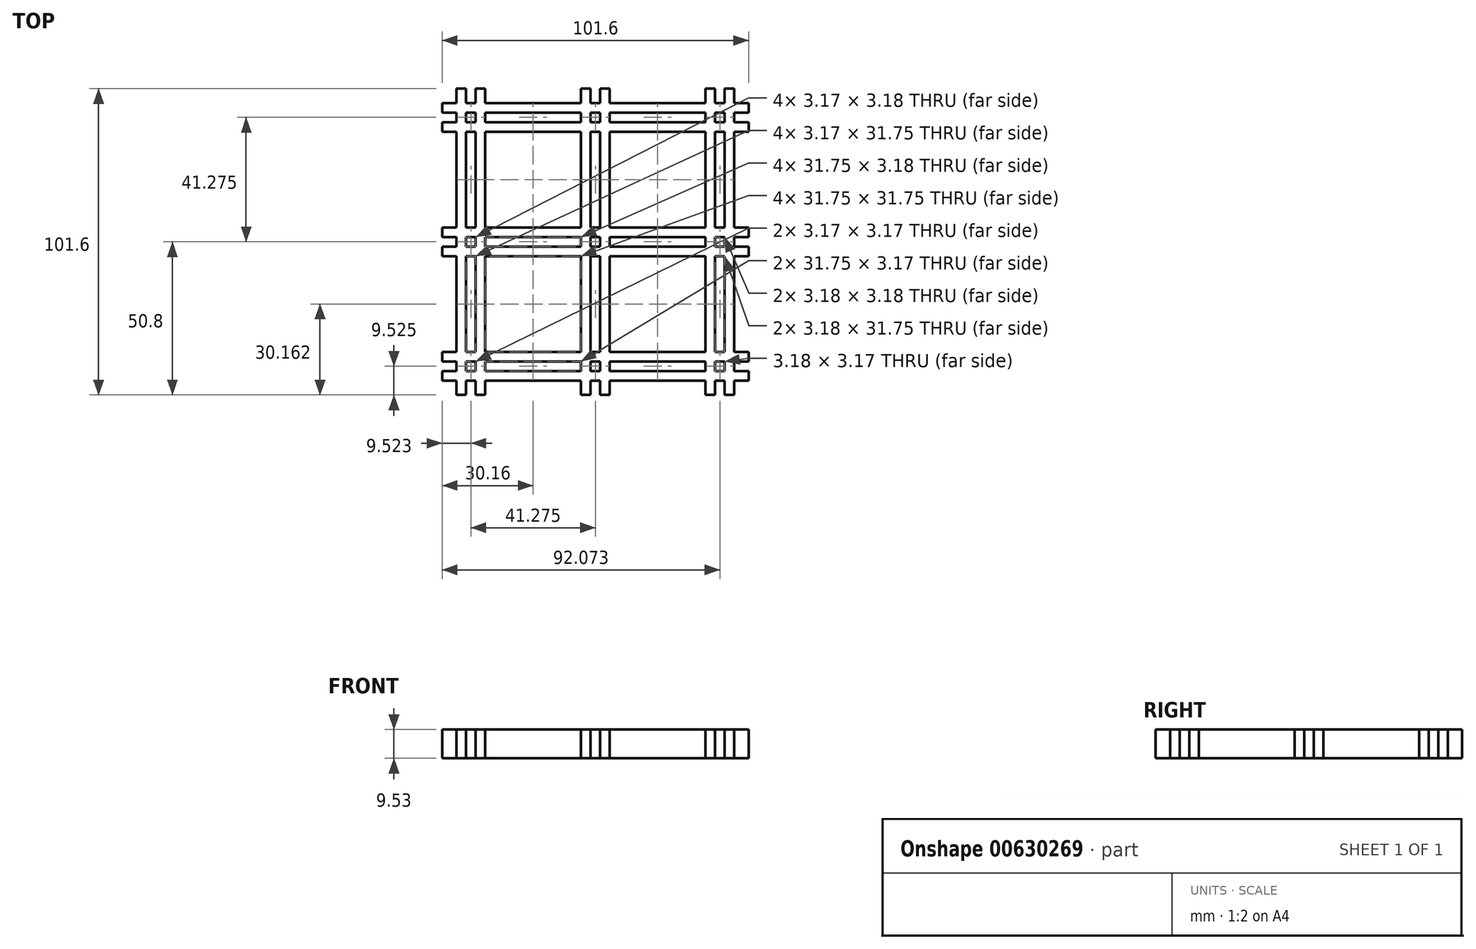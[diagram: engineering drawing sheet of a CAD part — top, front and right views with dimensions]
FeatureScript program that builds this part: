
annotation { "Feature Type Name" : "Feature", "Feature Type Description" : "" }
export const myFeature = defineFeature(function(context is Context, id is Id, definition is map)
    precondition{}
    {
        {
            var Q0;
            Q0=qCreatedBy(makeId("Top.planeOp"),FACE);
            var sketch = newSketch(context, id + "F0", { "sketchPlane" : qUnion([Q0])});
            skLineSegment(sketch, "E0.bottom", {"start": v(0, 0) * mm, "end": v(3.17, 0) * mm});
            skLineSegment(sketch, "E0.top", {"start": v(0, -101.6) * mm, "end": v(3.18, -101.6) * mm});
            skLineSegment(sketch, "E0.left", {"start": v(0, 0) * mm, "end": v(0, -101.6) * mm});
            skLineSegment(sketch, "E0.right", {"start": v(3.17, 0) * mm, "end": v(3.17, -101.6) * mm});
            skLineSegment(sketch, "E1.bottom", {"start": v(6.35, 0) * mm, "end": v(9.52, 0) * mm});
            skLineSegment(sketch, "E1.top", {"start": v(6.35, -101.6) * mm, "end": v(9.53, -101.6) * mm});
            skLineSegment(sketch, "E1.left", {"start": v(6.35, 0) * mm, "end": v(6.35, -101.6) * mm});
            skLineSegment(sketch, "E1.right", {"start": v(9.53, 0) * mm, "end": v(9.53, -101.6) * mm});
            skLineSegment(sketch, "E2.bottom", {"start": v(41.27, 0) * mm, "end": v(44.45, 0) * mm});
            skLineSegment(sketch, "E2.top", {"start": v(41.28, -101.6) * mm, "end": v(44.45, -101.6) * mm});
            skLineSegment(sketch, "E2.left", {"start": v(41.27, 0) * mm, "end": v(41.28, -101.6) * mm});
            skLineSegment(sketch, "E2.right", {"start": v(44.45, 0) * mm, "end": v(44.45, -101.6) * mm});
            skLineSegment(sketch, "E3", {"start": v(3.17, 0) * mm, "end": v(6.35, 0) * mm, "construction": true});
            skLineSegment(sketch, "E4", {"start": v(9.52, 0) * mm, "end": v(41.27, 0) * mm, "construction": true});
            skLineSegment(sketch, "E5.bottom", {"start": v(47.62, 0) * mm, "end": v(50.8, 0) * mm});
            skLineSegment(sketch, "E5.top", {"start": v(47.62, -101.6) * mm, "end": v(50.8, -101.6) * mm});
            skLineSegment(sketch, "E5.left", {"start": v(47.62, 0) * mm, "end": v(47.62, -101.6) * mm});
            skLineSegment(sketch, "E5.right", {"start": v(50.8, 0) * mm, "end": v(50.8, -101.6) * mm});
            skLineSegment(sketch, "E6.bottom", {"start": v(82.55, -101.6) * mm, "end": v(85.73, -101.6) * mm});
            skLineSegment(sketch, "E6.top", {"start": v(82.55, 0) * mm, "end": v(85.72, 0) * mm});
            skLineSegment(sketch, "E6.left", {"start": v(82.55, -101.6) * mm, "end": v(82.55, 0) * mm});
            skLineSegment(sketch, "E6.right", {"start": v(85.73, -101.6) * mm, "end": v(85.72, 0) * mm});
            skLineSegment(sketch, "E7.bottom", {"start": v(88.9, 0) * mm, "end": v(92.07, 0) * mm});
            skLineSegment(sketch, "E7.top", {"start": v(88.9, -101.6) * mm, "end": v(92.07, -101.6) * mm});
            skLineSegment(sketch, "E7.left", {"start": v(88.9, 0) * mm, "end": v(88.9, -101.6) * mm});
            skLineSegment(sketch, "E7.right", {"start": v(92.07, 0) * mm, "end": v(92.07, -101.6) * mm});
            skLineSegment(sketch, "E8", {"start": v(44.45, 0) * mm, "end": v(47.62, 0) * mm, "construction": true});
            skLineSegment(sketch, "E9", {"start": v(50.8, 0) * mm, "end": v(82.55, 0) * mm, "construction": true});
            skLineSegment(sketch, "E10", {"start": v(85.72, 0) * mm, "end": v(88.9, 0) * mm, "construction": true});
            skSolve(sketch);
        }
        {
            var Q0;
            Q0=qSketchRegion(id+"F0",true);
            extrude(context, id + "F1", {"entities" : qUnion([Q0]), "depth" : 9.52 * mm, "offsetDistance" : 25.4 * mm});
        }
        {
            var Q0;
            Q0=makeQuery(id+"F1.opExtrude","SWEPT_FACE",FACE,{"disambiguationData":[OSD([sQuery(id+"F0.wireOp",EDGE,"E7.right")])]});
            var sketch = newSketch(context, id + "F2", { "sketchPlane" : qUnion([Q0])});
            skLineSegment(sketch, "E11.bottom", {"start": v(-96.84, 0) * mm, "end": v(-93.66, 0) * mm});
            skLineSegment(sketch, "E11.top", {"start": v(-96.84, 4.76) * mm, "end": v(-93.66, 4.76) * mm});
            skLineSegment(sketch, "E11.left", {"start": v(-96.84, 0) * mm, "end": v(-96.84, 4.76) * mm});
            skLineSegment(sketch, "E11.right", {"start": v(-93.66, 0) * mm, "end": v(-93.66, 4.76) * mm});
            skLineSegment(sketch, "E12.top", {"start": v(-52.39, 4.76) * mm, "end": v(-49.21, 4.76) * mm, "construction": true});
            skLineSegment(sketch, "E12.left", {"start": v(-49.21, 0) * mm, "end": v(-49.21, 4.76) * mm});
            skLineSegment(sketch, "E12.right", {"start": v(-52.39, 0) * mm, "end": v(-52.39, 4.76) * mm});
            skLineSegment(sketch, "E13.bottom", {"start": v(-7.94, 0) * mm, "end": v(-4.76, 0) * mm});
            skLineSegment(sketch, "E13.top", {"start": v(-7.94, 4.76) * mm, "end": v(-4.76, 4.76) * mm});
            skLineSegment(sketch, "E13.left", {"start": v(-7.94, 0) * mm, "end": v(-7.94, 4.76) * mm});
            skLineSegment(sketch, "E13.right", {"start": v(-4.76, 0) * mm, "end": v(-4.76, 4.76) * mm});
            skLineSegment(sketch, "E14", {"start": v(-50.8, 4.76) * mm, "end": v(-50.8, 9.53) * mm, "construction": true});
            skLineSegment(sketch, "E15", {"start": v(-52.39, 4.76) * mm, "end": v(-55.56, 4.76) * mm});
            skLineSegment(sketch, "E16", {"start": v(-55.56, 4.76) * mm, "end": v(-55.56, 0) * mm});
            skLineSegment(sketch, "E17", {"start": v(-55.56, 0) * mm, "end": v(-52.39, 0) * mm});
            skLineSegment(sketch, "E18", {"start": v(-49.21, 0) * mm, "end": v(-46.04, 0) * mm});
            skLineSegment(sketch, "E19", {"start": v(-46.04, 0) * mm, "end": v(-46.04, 4.76) * mm});
            skLineSegment(sketch, "E20", {"start": v(-46.04, 4.76) * mm, "end": v(-49.21, 4.76) * mm});
            skLineSegment(sketch, "E21.bottom", {"start": v(-11.11, 4.76) * mm, "end": v(-14.29, 4.76) * mm});
            skLineSegment(sketch, "E21.top", {"start": v(-11.11, 0) * mm, "end": v(-14.29, 0) * mm});
            skLineSegment(sketch, "E21.left", {"start": v(-11.11, 4.76) * mm, "end": v(-11.11, 0) * mm});
            skLineSegment(sketch, "E21.right", {"start": v(-14.29, 4.76) * mm, "end": v(-14.29, 0) * mm});
            skPoint(sketch, "E22.firstSnap0", {"position": v(-95.25, 4.76) * mm});
            skLineSegment(sketch, "E22.bottom", {"start": v(-90.49, 4.76) * mm, "end": v(-87.31, 4.76) * mm});
            skLineSegment(sketch, "E22.top", {"start": v(-90.49, 0) * mm, "end": v(-87.31, 0) * mm});
            skLineSegment(sketch, "E22.left", {"start": v(-90.49, 4.76) * mm, "end": v(-90.49, 0) * mm});
            skLineSegment(sketch, "E22.right", {"start": v(-87.31, 4.76) * mm, "end": v(-87.31, 0) * mm});
            skLineSegment(sketch, "E23", {"start": v(-93.66, 0) * mm, "end": v(-90.49, 0) * mm, "construction": true});
            skLineSegment(sketch, "E24", {"start": v(-11.11, 0) * mm, "end": v(-7.94, 0) * mm, "construction": true});
            skSolve(sketch);
        }
        {
            var Q0;
            Q0=qSketchRegion(id+"F2",true);
            extrude(context, id + "F3", {"entities" : qUnion([Q0]), "operationType" : NewBodyOperationType.REMOVE, "endBound" : BoundingType.THROUGH_ALL, "oppositeDirection" : true, "depth" : 25.4 * mm, "offsetDistance" : 25.4 * mm});
        }
        {
            var Q0;
            Q0=qCreatedBy(makeId("Top.planeOp"),FACE);
            var sketch = newSketch(context, id + "F4", { "sketchPlane" : qUnion([Q0])});
            skLineSegment(sketch, "E25.bottom", {"start": v(96.84, -7.94) * mm, "end": v(-4.76, -7.94) * mm});
            skLineSegment(sketch, "E25.top", {"start": v(96.84, -4.76) * mm, "end": v(-4.76, -4.76) * mm});
            skLineSegment(sketch, "E25.left", {"start": v(96.84, -7.94) * mm, "end": v(96.84, -4.76) * mm});
            skLineSegment(sketch, "E25.right", {"start": v(-4.76, -7.94) * mm, "end": v(-4.76, -4.76) * mm});
            skLineSegment(sketch, "E26.bottom", {"start": v(96.84, -14.29) * mm, "end": v(-4.76, -14.29) * mm});
            skLineSegment(sketch, "E26.top", {"start": v(96.84, -11.11) * mm, "end": v(-4.76, -11.11) * mm});
            skLineSegment(sketch, "E26.left", {"start": v(96.84, -14.29) * mm, "end": v(96.84, -11.11) * mm});
            skLineSegment(sketch, "E26.right", {"start": v(-4.76, -14.29) * mm, "end": v(-4.76, -11.11) * mm});
            skLineSegment(sketch, "E27.bottom", {"start": v(96.84, -96.84) * mm, "end": v(-4.76, -96.84) * mm});
            skLineSegment(sketch, "E27.top", {"start": v(96.84, -93.66) * mm, "end": v(-4.76, -93.66) * mm});
            skLineSegment(sketch, "E27.left", {"start": v(96.84, -96.84) * mm, "end": v(96.84, -93.66) * mm});
            skLineSegment(sketch, "E27.right", {"start": v(-4.76, -96.84) * mm, "end": v(-4.76, -93.66) * mm});
            skLineSegment(sketch, "E28.bottom", {"start": v(-4.76, -46.04) * mm, "end": v(96.84, -46.04) * mm});
            skLineSegment(sketch, "E28.top", {"start": v(-4.76, -49.21) * mm, "end": v(96.84, -49.21) * mm});
            skLineSegment(sketch, "E28.left", {"start": v(-4.76, -46.04) * mm, "end": v(-4.76, -49.21) * mm});
            skLineSegment(sketch, "E28.right", {"start": v(96.84, -46.04) * mm, "end": v(96.84, -49.21) * mm});
            skLineSegment(sketch, "E29.bottom", {"start": v(96.84, -55.56) * mm, "end": v(-4.76, -55.56) * mm});
            skLineSegment(sketch, "E29.top", {"start": v(96.84, -52.39) * mm, "end": v(-4.76, -52.39) * mm});
            skLineSegment(sketch, "E29.left", {"start": v(96.84, -55.56) * mm, "end": v(96.84, -52.39) * mm});
            skLineSegment(sketch, "E29.right", {"start": v(-4.76, -55.56) * mm, "end": v(-4.76, -52.39) * mm});
            skLineSegment(sketch, "E30.bottom", {"start": v(-4.76, -87.31) * mm, "end": v(96.84, -87.31) * mm});
            skLineSegment(sketch, "E30.top", {"start": v(-4.76, -90.49) * mm, "end": v(96.84, -90.49) * mm});
            skLineSegment(sketch, "E30.left", {"start": v(-4.76, -87.31) * mm, "end": v(-4.76, -90.49) * mm});
            skLineSegment(sketch, "E30.right", {"start": v(96.84, -87.31) * mm, "end": v(96.84, -90.49) * mm});
            skLineSegment(sketch, "E31", {"start": v(47.62, 0) * mm, "end": v(44.45, 0) * mm, "construction": true});
            skLineSegment(sketch, "E32", {"start": v(46.04, 0) * mm, "end": v(46.04, -4.76) * mm, "construction": true});
            skSolve(sketch);
        }
        {
            var Q0;
            Q0=qSketchRegion(id+"F4",true);
            var Q1;
            Q1=makeQuery(id+"F3.boolean.opBoolean","COPY",FACE,{"disambiguationData":[TD([makeQuery(id+"F1.opExtrude","SWEPT_FACE",FACE,{"disambiguationData":[OSD([sQuery(id+"F0.wireOp",EDGE,"E1.left")])]})])],"derivedFrom":makeQuery(id+"F3.opExtrude","SWEPT_FACE",FACE,{"disambiguationData":[OSD([sQuery(id+"F2.wireOp",EDGE,"E13.top")])]})});
            extrude(context, id + "F5", {"entities" : qUnion([Q0]), "endBound" : BoundingType.UP_TO_SURFACE, "depth" : 25.4 * mm, "endBoundEntityFace" : qUnion([Q1]), "offsetDistance" : 25.4 * mm});
        }
        {
            var Q0;
            Q0=makeQuery(id+"F5.opExtrude","CAP_FACE",FACE,{"disambiguationData":[OSD([sQuery(id+"F4.wireOp",EDGE,"E25.bottom"),sQuery(id+"F4.wireOp",EDGE,"E25.top"),sQuery(id+"F4.wireOp",EDGE,"E25.left"),sQuery(id+"F4.wireOp",EDGE,"E25.right")])],"isStart":false});
            var sketch = newSketch(context, id + "F6", { "sketchPlane" : qUnion([Q0])});
            skLineSegment(sketch, "E33.bottom", {"start": v(3.18, -4.76) * mm, "end": v(6.35, -4.76) * mm});
            skLineSegment(sketch, "E33.top", {"start": v(3.18, -7.94) * mm, "end": v(6.35, -7.94) * mm});
            skLineSegment(sketch, "E33.left", {"start": v(3.17, -4.76) * mm, "end": v(3.17, -7.94) * mm});
            skLineSegment(sketch, "E33.right", {"start": v(6.35, -4.76) * mm, "end": v(6.35, -7.94) * mm});
            skLineSegment(sketch, "E34.bottom", {"start": v(3.17, -11.11) * mm, "end": v(6.35, -11.11) * mm});
            skLineSegment(sketch, "E34.top", {"start": v(3.17, -14.29) * mm, "end": v(6.35, -14.29) * mm});
            skLineSegment(sketch, "E34.left", {"start": v(3.17, -11.11) * mm, "end": v(3.17, -14.29) * mm});
            skLineSegment(sketch, "E34.right", {"start": v(6.35, -11.11) * mm, "end": v(6.35, -14.29) * mm});
            skLineSegment(sketch, "E35.bottom", {"start": v(3.18, -93.66) * mm, "end": v(6.35, -93.66) * mm});
            skLineSegment(sketch, "E35.top", {"start": v(3.18, -96.84) * mm, "end": v(6.35, -96.84) * mm});
            skLineSegment(sketch, "E35.left", {"start": v(3.17, -93.66) * mm, "end": v(3.18, -96.84) * mm});
            skLineSegment(sketch, "E35.right", {"start": v(6.35, -93.66) * mm, "end": v(6.35, -96.84) * mm});
            skLineSegment(sketch, "E36.bottom", {"start": v(41.28, -96.84) * mm, "end": v(9.53, -96.84) * mm});
            skLineSegment(sketch, "E36.top", {"start": v(41.28, -93.66) * mm, "end": v(9.53, -93.66) * mm});
            skLineSegment(sketch, "E36.left", {"start": v(41.28, -96.84) * mm, "end": v(41.28, -93.66) * mm});
            skLineSegment(sketch, "E36.right", {"start": v(9.53, -96.84) * mm, "end": v(9.53, -93.66) * mm});
            skLineSegment(sketch, "E37.bottom", {"start": v(41.27, -14.29) * mm, "end": v(9.52, -14.29) * mm});
            skLineSegment(sketch, "E37.top", {"start": v(41.27, -11.11) * mm, "end": v(9.52, -11.11) * mm});
            skLineSegment(sketch, "E37.left", {"start": v(41.27, -14.29) * mm, "end": v(41.27, -11.11) * mm});
            skLineSegment(sketch, "E37.right", {"start": v(9.52, -14.29) * mm, "end": v(9.52, -11.11) * mm});
            skLineSegment(sketch, "E38.bottom", {"start": v(41.27, -4.76) * mm, "end": v(9.53, -4.76) * mm});
            skLineSegment(sketch, "E38.top", {"start": v(41.27, -7.94) * mm, "end": v(9.53, -7.94) * mm});
            skLineSegment(sketch, "E38.left", {"start": v(41.27, -4.76) * mm, "end": v(41.27, -7.94) * mm});
            skLineSegment(sketch, "E38.right", {"start": v(9.53, -4.76) * mm, "end": v(9.53, -7.94) * mm});
            skLineSegment(sketch, "E39.bottom", {"start": v(96.84, -4.76) * mm, "end": v(92.07, -4.76) * mm});
            skLineSegment(sketch, "E39.top", {"start": v(96.84, -7.94) * mm, "end": v(92.07, -7.94) * mm});
            skLineSegment(sketch, "E39.left", {"start": v(96.84, -4.76) * mm, "end": v(96.84, -7.94) * mm});
            skLineSegment(sketch, "E39.right", {"start": v(92.07, -4.76) * mm, "end": v(92.07, -7.94) * mm});
            skLineSegment(sketch, "E40.bottom", {"start": v(96.84, -11.11) * mm, "end": v(92.07, -11.11) * mm});
            skLineSegment(sketch, "E40.top", {"start": v(96.84, -14.29) * mm, "end": v(92.07, -14.29) * mm});
            skLineSegment(sketch, "E40.left", {"start": v(96.84, -11.11) * mm, "end": v(96.84, -14.29) * mm});
            skLineSegment(sketch, "E40.right", {"start": v(92.07, -11.11) * mm, "end": v(92.07, -14.29) * mm});
            skLineSegment(sketch, "E41.bottom", {"start": v(96.84, -93.66) * mm, "end": v(92.07, -93.66) * mm});
            skLineSegment(sketch, "E41.top", {"start": v(96.84, -96.84) * mm, "end": v(92.07, -96.84) * mm});
            skLineSegment(sketch, "E41.left", {"start": v(96.84, -93.66) * mm, "end": v(96.84, -96.84) * mm});
            skLineSegment(sketch, "E41.right", {"start": v(92.07, -93.66) * mm, "end": v(92.07, -96.84) * mm});
            skLineSegment(sketch, "E42.bottom", {"start": v(0, -93.66) * mm, "end": v(-4.76, -93.66) * mm});
            skLineSegment(sketch, "E42.top", {"start": v(0, -96.84) * mm, "end": v(-4.76, -96.84) * mm});
            skLineSegment(sketch, "E42.left", {"start": v(0, -93.66) * mm, "end": v(0, -96.84) * mm});
            skLineSegment(sketch, "E42.right", {"start": v(-4.76, -93.66) * mm, "end": v(-4.76, -96.84) * mm});
            skLineSegment(sketch, "E43.bottom", {"start": v(0, -11.11) * mm, "end": v(-4.76, -11.11) * mm});
            skLineSegment(sketch, "E43.top", {"start": v(0, -14.29) * mm, "end": v(-4.76, -14.29) * mm});
            skLineSegment(sketch, "E43.left", {"start": v(0, -11.11) * mm, "end": v(0, -14.29) * mm});
            skLineSegment(sketch, "E43.right", {"start": v(-4.76, -11.11) * mm, "end": v(-4.76, -14.29) * mm});
            skLineSegment(sketch, "E44.bottom", {"start": v(0, -4.76) * mm, "end": v(-4.76, -4.76) * mm});
            skLineSegment(sketch, "E44.top", {"start": v(0, -7.94) * mm, "end": v(-4.76, -7.94) * mm});
            skLineSegment(sketch, "E44.left", {"start": v(0, -4.76) * mm, "end": v(0, -7.94) * mm});
            skLineSegment(sketch, "E44.right", {"start": v(-4.76, -4.76) * mm, "end": v(-4.76, -7.94) * mm});
            skLineSegment(sketch, "E45.bottom", {"start": v(-4.76, -46.04) * mm, "end": v(0, -46.04) * mm});
            skLineSegment(sketch, "E45.top", {"start": v(-4.76, -49.21) * mm, "end": v(0, -49.21) * mm});
            skLineSegment(sketch, "E45.left", {"start": v(-4.76, -46.04) * mm, "end": v(-4.76, -49.21) * mm});
            skLineSegment(sketch, "E45.right", {"start": v(0, -46.04) * mm, "end": v(0, -49.21) * mm});
            skLineSegment(sketch, "E46.bottom", {"start": v(0, -52.39) * mm, "end": v(-4.76, -52.39) * mm});
            skLineSegment(sketch, "E46.top", {"start": v(0, -55.56) * mm, "end": v(-4.76, -55.56) * mm});
            skLineSegment(sketch, "E46.left", {"start": v(0, -52.39) * mm, "end": v(0, -55.56) * mm});
            skLineSegment(sketch, "E46.right", {"start": v(-4.76, -52.39) * mm, "end": v(-4.76, -55.56) * mm});
            skLineSegment(sketch, "E47.bottom", {"start": v(-4.76, -87.31) * mm, "end": v(0, -87.31) * mm});
            skLineSegment(sketch, "E47.top", {"start": v(-4.76, -90.49) * mm, "end": v(0, -90.49) * mm});
            skLineSegment(sketch, "E47.left", {"start": v(-4.76, -87.31) * mm, "end": v(-4.76, -90.49) * mm});
            skLineSegment(sketch, "E47.right", {"start": v(0, -87.31) * mm, "end": v(0, -90.49) * mm});
            skLineSegment(sketch, "E48.bottom", {"start": v(6.35, -46.04) * mm, "end": v(3.17, -46.04) * mm});
            skLineSegment(sketch, "E48.top", {"start": v(6.35, -49.21) * mm, "end": v(3.17, -49.21) * mm});
            skLineSegment(sketch, "E48.left", {"start": v(6.35, -46.04) * mm, "end": v(6.35, -49.21) * mm});
            skLineSegment(sketch, "E48.right", {"start": v(3.17, -46.04) * mm, "end": v(3.17, -49.21) * mm});
            skLineSegment(sketch, "E49.bottom", {"start": v(6.35, -52.39) * mm, "end": v(3.18, -52.39) * mm});
            skLineSegment(sketch, "E49.top", {"start": v(6.35, -55.56) * mm, "end": v(3.17, -55.56) * mm});
            skLineSegment(sketch, "E49.left", {"start": v(6.35, -52.39) * mm, "end": v(6.35, -55.56) * mm});
            skLineSegment(sketch, "E49.right", {"start": v(3.18, -52.39) * mm, "end": v(3.18, -55.56) * mm});
            skLineSegment(sketch, "E50.bottom", {"start": v(6.35, -87.31) * mm, "end": v(3.18, -87.31) * mm});
            skLineSegment(sketch, "E50.top", {"start": v(6.35, -90.49) * mm, "end": v(3.18, -90.49) * mm});
            skLineSegment(sketch, "E50.left", {"start": v(6.35, -87.31) * mm, "end": v(6.35, -90.49) * mm});
            skLineSegment(sketch, "E50.right", {"start": v(3.18, -87.31) * mm, "end": v(3.18, -90.49) * mm});
            skLineSegment(sketch, "E51.bottom", {"start": v(9.53, -46.04) * mm, "end": v(41.27, -46.04) * mm});
            skLineSegment(sketch, "E51.top", {"start": v(9.53, -49.21) * mm, "end": v(41.27, -49.21) * mm});
            skLineSegment(sketch, "E51.left", {"start": v(9.53, -46.04) * mm, "end": v(9.53, -49.21) * mm});
            skLineSegment(sketch, "E51.right", {"start": v(41.27, -46.04) * mm, "end": v(41.27, -49.21) * mm});
            skLineSegment(sketch, "E52.bottom", {"start": v(9.53, -52.39) * mm, "end": v(41.27, -52.39) * mm});
            skLineSegment(sketch, "E52.top", {"start": v(9.53, -55.56) * mm, "end": v(41.27, -55.56) * mm});
            skLineSegment(sketch, "E52.left", {"start": v(9.53, -52.39) * mm, "end": v(9.53, -55.56) * mm});
            skLineSegment(sketch, "E52.right", {"start": v(41.27, -52.39) * mm, "end": v(41.27, -55.56) * mm});
            skLineSegment(sketch, "E53.bottom", {"start": v(9.53, -87.31) * mm, "end": v(41.28, -87.31) * mm});
            skLineSegment(sketch, "E53.top", {"start": v(9.53, -90.49) * mm, "end": v(41.28, -90.49) * mm});
            skLineSegment(sketch, "E53.left", {"start": v(9.53, -87.31) * mm, "end": v(9.53, -90.49) * mm});
            skLineSegment(sketch, "E53.right", {"start": v(41.28, -87.31) * mm, "end": v(41.28, -90.49) * mm});
            skPoint(sketch, "E54.oppositeSnap0", {"position": v(47.62, -9.08) * mm});
            skLineSegment(sketch, "E54.bottom", {"start": v(44.45, -4.76) * mm, "end": v(47.62, -4.76) * mm});
            skLineSegment(sketch, "E54.top", {"start": v(44.45, -7.94) * mm, "end": v(47.62, -7.94) * mm});
            skLineSegment(sketch, "E54.left", {"start": v(44.45, -4.76) * mm, "end": v(44.45, -7.94) * mm});
            skLineSegment(sketch, "E54.right", {"start": v(47.62, -4.76) * mm, "end": v(47.62, -7.94) * mm});
            skLineSegment(sketch, "E55.bottom", {"start": v(47.62, -55.56) * mm, "end": v(44.45, -55.56) * mm});
            skLineSegment(sketch, "E55.top", {"start": v(47.62, -52.39) * mm, "end": v(44.45, -52.39) * mm});
            skLineSegment(sketch, "E55.left", {"start": v(47.62, -55.56) * mm, "end": v(47.62, -52.39) * mm});
            skLineSegment(sketch, "E55.right", {"start": v(44.45, -55.56) * mm, "end": v(44.45, -52.39) * mm});
            skLineSegment(sketch, "E56.bottom", {"start": v(47.62, -11.11) * mm, "end": v(44.45, -11.11) * mm});
            skLineSegment(sketch, "E56.top", {"start": v(47.62, -14.29) * mm, "end": v(44.45, -14.29) * mm});
            skLineSegment(sketch, "E56.left", {"start": v(47.62, -11.11) * mm, "end": v(47.62, -14.29) * mm});
            skLineSegment(sketch, "E56.right", {"start": v(44.45, -11.11) * mm, "end": v(44.45, -14.29) * mm});
            skLineSegment(sketch, "E57.bottom", {"start": v(47.62, -46.04) * mm, "end": v(44.45, -46.04) * mm});
            skLineSegment(sketch, "E57.top", {"start": v(47.63, -49.21) * mm, "end": v(44.45, -49.21) * mm});
            skLineSegment(sketch, "E57.left", {"start": v(47.63, -46.04) * mm, "end": v(47.63, -49.21) * mm});
            skLineSegment(sketch, "E57.right", {"start": v(44.45, -46.04) * mm, "end": v(44.45, -49.21) * mm});
            skLineSegment(sketch, "E58.bottom", {"start": v(47.62, -87.31) * mm, "end": v(44.45, -87.31) * mm});
            skLineSegment(sketch, "E58.top", {"start": v(47.63, -90.49) * mm, "end": v(44.45, -90.49) * mm});
            skLineSegment(sketch, "E58.left", {"start": v(47.63, -87.31) * mm, "end": v(47.63, -90.49) * mm});
            skLineSegment(sketch, "E58.right", {"start": v(44.45, -87.31) * mm, "end": v(44.45, -90.49) * mm});
            skLineSegment(sketch, "E59.bottom", {"start": v(47.62, -93.66) * mm, "end": v(44.45, -93.66) * mm});
            skLineSegment(sketch, "E59.top", {"start": v(47.62, -96.84) * mm, "end": v(44.45, -96.84) * mm});
            skLineSegment(sketch, "E59.left", {"start": v(47.62, -93.66) * mm, "end": v(47.62, -96.84) * mm});
            skLineSegment(sketch, "E59.right", {"start": v(44.45, -93.66) * mm, "end": v(44.45, -96.84) * mm});
            skLineSegment(sketch, "E60.bottom", {"start": v(85.72, -4.76) * mm, "end": v(88.9, -4.76) * mm});
            skLineSegment(sketch, "E60.top", {"start": v(85.72, -7.94) * mm, "end": v(88.9, -7.94) * mm});
            skLineSegment(sketch, "E60.left", {"start": v(85.72, -4.76) * mm, "end": v(85.72, -7.94) * mm});
            skLineSegment(sketch, "E60.right", {"start": v(88.9, -4.76) * mm, "end": v(88.9, -7.94) * mm});
            skLineSegment(sketch, "E61.bottom", {"start": v(85.72, -11.11) * mm, "end": v(88.9, -11.11) * mm});
            skLineSegment(sketch, "E61.top", {"start": v(85.72, -14.29) * mm, "end": v(88.9, -14.29) * mm});
            skLineSegment(sketch, "E61.left", {"start": v(85.72, -11.11) * mm, "end": v(85.72, -14.29) * mm});
            skLineSegment(sketch, "E61.right", {"start": v(88.9, -11.11) * mm, "end": v(88.9, -14.29) * mm});
            skLineSegment(sketch, "E62.bottom", {"start": v(92.07, -46.04) * mm, "end": v(96.84, -46.04) * mm});
            skLineSegment(sketch, "E62.top", {"start": v(92.07, -49.21) * mm, "end": v(96.84, -49.21) * mm});
            skLineSegment(sketch, "E62.left", {"start": v(92.07, -46.04) * mm, "end": v(92.07, -49.21) * mm});
            skLineSegment(sketch, "E62.right", {"start": v(96.84, -46.04) * mm, "end": v(96.84, -49.21) * mm});
            skLineSegment(sketch, "E63.bottom", {"start": v(85.72, -52.39) * mm, "end": v(88.9, -52.39) * mm});
            skLineSegment(sketch, "E63.top", {"start": v(85.72, -55.56) * mm, "end": v(88.9, -55.56) * mm});
            skLineSegment(sketch, "E63.left", {"start": v(85.72, -52.39) * mm, "end": v(85.72, -55.56) * mm});
            skLineSegment(sketch, "E63.right", {"start": v(88.9, -52.39) * mm, "end": v(88.9, -55.56) * mm});
            skLineSegment(sketch, "E64.bottom", {"start": v(92.07, -52.39) * mm, "end": v(96.84, -52.39) * mm});
            skLineSegment(sketch, "E64.top", {"start": v(92.07, -55.56) * mm, "end": v(96.84, -55.56) * mm});
            skLineSegment(sketch, "E64.left", {"start": v(92.07, -52.39) * mm, "end": v(92.07, -55.56) * mm});
            skLineSegment(sketch, "E64.right", {"start": v(96.84, -52.39) * mm, "end": v(96.84, -55.56) * mm});
            skLineSegment(sketch, "E65.bottom", {"start": v(85.72, -87.31) * mm, "end": v(88.9, -87.31) * mm});
            skLineSegment(sketch, "E65.top", {"start": v(85.72, -90.49) * mm, "end": v(88.9, -90.49) * mm});
            skLineSegment(sketch, "E65.left", {"start": v(85.72, -87.31) * mm, "end": v(85.72, -90.49) * mm});
            skLineSegment(sketch, "E65.right", {"start": v(88.9, -87.31) * mm, "end": v(88.9, -90.49) * mm});
            skLineSegment(sketch, "E66.bottom", {"start": v(85.72, -46.04) * mm, "end": v(88.9, -46.04) * mm});
            skLineSegment(sketch, "E66.top", {"start": v(85.72, -49.21) * mm, "end": v(88.9, -49.21) * mm});
            skLineSegment(sketch, "E66.left", {"start": v(85.72, -46.04) * mm, "end": v(85.72, -49.21) * mm});
            skLineSegment(sketch, "E66.right", {"start": v(88.9, -46.04) * mm, "end": v(88.9, -49.21) * mm});
            skLineSegment(sketch, "E67.bottom", {"start": v(85.73, -93.66) * mm, "end": v(88.9, -93.66) * mm});
            skLineSegment(sketch, "E67.top", {"start": v(85.73, -96.84) * mm, "end": v(88.9, -96.84) * mm});
            skLineSegment(sketch, "E67.left", {"start": v(85.72, -93.66) * mm, "end": v(85.72, -96.84) * mm});
            skLineSegment(sketch, "E67.right", {"start": v(88.9, -93.66) * mm, "end": v(88.9, -96.84) * mm});
            skLineSegment(sketch, "E68.bottom", {"start": v(92.07, -87.31) * mm, "end": v(96.84, -87.31) * mm});
            skLineSegment(sketch, "E68.top", {"start": v(92.07, -90.49) * mm, "end": v(96.84, -90.49) * mm});
            skLineSegment(sketch, "E68.left", {"start": v(92.07, -87.31) * mm, "end": v(92.07, -90.49) * mm});
            skLineSegment(sketch, "E68.right", {"start": v(96.84, -87.31) * mm, "end": v(96.84, -90.49) * mm});
            skLineSegment(sketch, "E69.bottom", {"start": v(50.8, -96.84) * mm, "end": v(82.55, -96.84) * mm});
            skLineSegment(sketch, "E69.top", {"start": v(50.8, -93.66) * mm, "end": v(82.55, -93.66) * mm});
            skLineSegment(sketch, "E69.left", {"start": v(50.8, -96.84) * mm, "end": v(50.8, -93.66) * mm});
            skLineSegment(sketch, "E69.right", {"start": v(82.55, -96.84) * mm, "end": v(82.55, -93.66) * mm});
            skLineSegment(sketch, "E70.bottom", {"start": v(50.8, -87.31) * mm, "end": v(82.55, -87.31) * mm});
            skLineSegment(sketch, "E70.top", {"start": v(50.8, -90.49) * mm, "end": v(82.55, -90.49) * mm});
            skLineSegment(sketch, "E70.left", {"start": v(50.8, -87.31) * mm, "end": v(50.8, -90.49) * mm});
            skLineSegment(sketch, "E70.right", {"start": v(82.55, -87.31) * mm, "end": v(82.55, -90.49) * mm});
            skLineSegment(sketch, "E71.bottom", {"start": v(50.8, -55.56) * mm, "end": v(82.55, -55.56) * mm});
            skLineSegment(sketch, "E71.top", {"start": v(50.8, -52.39) * mm, "end": v(82.55, -52.39) * mm});
            skLineSegment(sketch, "E71.left", {"start": v(50.8, -55.56) * mm, "end": v(50.8, -52.39) * mm});
            skLineSegment(sketch, "E71.right", {"start": v(82.55, -55.56) * mm, "end": v(82.55, -52.39) * mm});
            skLineSegment(sketch, "E72.bottom", {"start": v(50.8, -46.04) * mm, "end": v(82.55, -46.04) * mm});
            skLineSegment(sketch, "E72.top", {"start": v(50.8, -49.21) * mm, "end": v(82.55, -49.21) * mm});
            skLineSegment(sketch, "E72.left", {"start": v(50.8, -46.04) * mm, "end": v(50.8, -49.21) * mm});
            skLineSegment(sketch, "E72.right", {"start": v(82.55, -46.04) * mm, "end": v(82.55, -49.21) * mm});
            skLineSegment(sketch, "E73.bottom", {"start": v(82.55, -14.29) * mm, "end": v(50.8, -14.29) * mm});
            skLineSegment(sketch, "E73.top", {"start": v(82.55, -11.11) * mm, "end": v(50.8, -11.11) * mm});
            skLineSegment(sketch, "E73.left", {"start": v(82.55, -14.29) * mm, "end": v(82.55, -11.11) * mm});
            skLineSegment(sketch, "E73.right", {"start": v(50.8, -14.29) * mm, "end": v(50.8, -11.11) * mm});
            skLineSegment(sketch, "E74.bottom", {"start": v(50.8, -7.94) * mm, "end": v(82.55, -7.94) * mm});
            skLineSegment(sketch, "E74.top", {"start": v(50.8, -4.76) * mm, "end": v(82.55, -4.76) * mm});
            skLineSegment(sketch, "E74.left", {"start": v(50.8, -7.94) * mm, "end": v(50.8, -4.76) * mm});
            skLineSegment(sketch, "E74.right", {"start": v(82.55, -7.94) * mm, "end": v(82.55, -4.76) * mm});
            skSolve(sketch);
        }
        {
            var Q0;
            Q0=qSketchRegion(id+"F6",true);
            var Q1;
            Q1=makeQuery(id+"F1.opExtrude","CAP_FACE",FACE,{"disambiguationData":[OSD([sQuery(id+"F0.wireOp",EDGE,"E1.bottom"),sQuery(id+"F0.wireOp",EDGE,"E1.top"),sQuery(id+"F0.wireOp",EDGE,"E1.left"),sQuery(id+"F0.wireOp",EDGE,"E1.right")])],"isStart":false});
            extrude(context, id + "F7", {"entities" : qUnion([Q0]), "operationType" : NewBodyOperationType.ADD, "endBound" : BoundingType.UP_TO_SURFACE, "depth" : 25.4 * mm, "endBoundEntityFace" : qUnion([Q1]), "offsetDistance" : 25.4 * mm});
        }
    });
